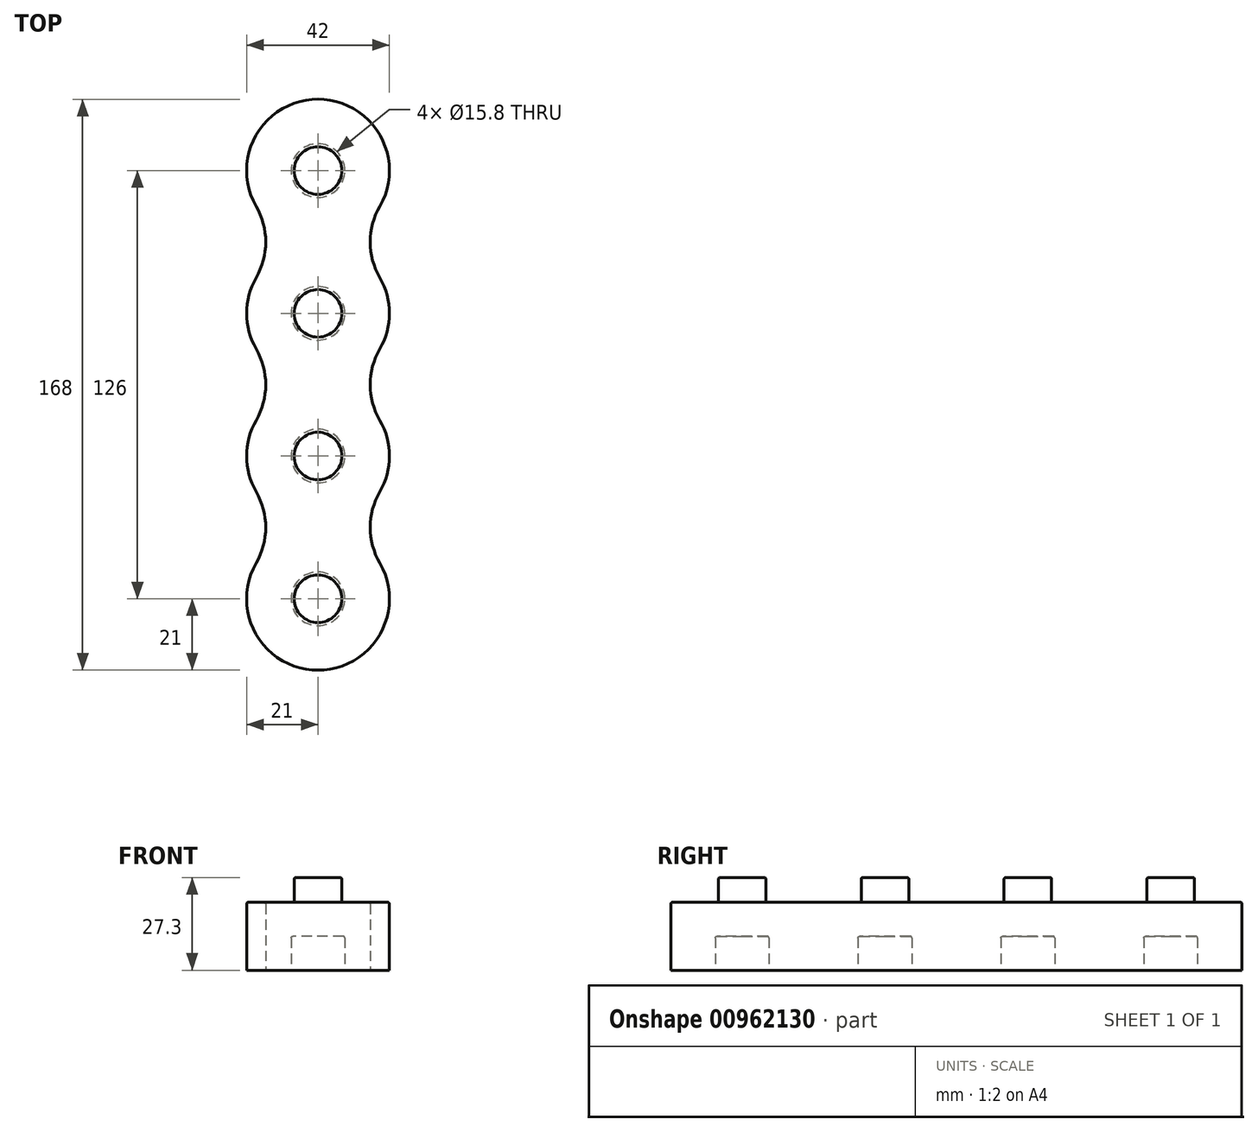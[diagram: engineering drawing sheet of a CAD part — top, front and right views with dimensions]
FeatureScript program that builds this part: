
annotation { "Feature Type Name" : "Feature", "Feature Type Description" : "" }
export const myFeature = defineFeature(function(context is Context, id is Id, definition is map)
    precondition{}
    {
        {
            assignVariable(context, id + "F0", {"name" : "inner_circle_extrude", "anyValue" : 10});
        }
        {
            assignVariable(context, id + "F1", {"name" : "nipple_circle_extrude", "anyValue" : 7.3});
        }
        {
            assignVariable(context, id + "F2", {"name" : "outer_circle_extrude", "anyValue" : 20});
        }
        {
            assignVariable(context, id + "F3", {"name" : "fillet", "anyValue" : 0.5});
        }
        {
            var Q0;
            Q0=qCreatedBy(makeId("Top.planeOp"),FACE);
            var sketch = newSketch(context, id + "F4", { "sketchPlane" : qUnion([Q0])});
            skCircle(sketch, "E0", {"center": v(0, 42) * mm, "radius": 7.9 * mm});
            skCircle(sketch, "E1", {"center": v(0, 0) * mm, "radius": 7.9 * mm});
            skArc(sketch, "E2.converted", {"start": v(18.19, 31.5) * mm, "mid": v(21, 42) * mm, "end": v(18.19, 52.5) * mm});
            skArc(sketch, "E3.converted", {"start": v(-18.19, 10.5) * mm, "mid": v(0, -21) * mm, "end": v(18.19, 10.5) * mm});
            skPoint(sketch, "E4.orphan", {"position": v(-18.87, 9.22) * mm});
            skArc(sketch, "E5", {"start": v(-18.19, 10.5) * mm, "mid": v(-15.37, 21) * mm, "end": v(-18.19, 31.5) * mm});
            skArc(sketch, "E6.MirrorC", {"start": v(18.19, 10.5) * mm, "mid": v(15.37, 21) * mm, "end": v(18.19, 31.5) * mm});
            skArc(sketch, "E7", {"start": v(-18.19, 94.5) * mm, "mid": v(-21, 84) * mm, "end": v(-18.19, 73.5) * mm});
            skArc(sketch, "E8", {"start": v(-18.19, 52.5) * mm, "mid": v(-15.37, 63) * mm, "end": v(-18.19, 73.5) * mm});
            skArc(sketch, "E9", {"start": v(18.19, 73.5) * mm, "mid": v(15.37, 63) * mm, "end": v(18.19, 52.5) * mm});
            skArc(sketch, "E10", {"start": v(18.19, 115.5) * mm, "mid": v(0, 147) * mm, "end": v(-18.19, 115.5) * mm});
            skArc(sketch, "E11", {"start": v(-18.19, 94.5) * mm, "mid": v(-15.37, 105) * mm, "end": v(-18.19, 115.5) * mm});
            skArc(sketch, "E12", {"start": v(18.19, 115.5) * mm, "mid": v(15.37, 105) * mm, "end": v(18.19, 94.5) * mm});
            skCircle(sketch, "E13", {"center": v(0, 84) * mm, "radius": 7.9 * mm});
            skCircle(sketch, "E14", {"center": v(0, 126) * mm, "radius": 7.9 * mm});
            skArc(sketch, "E15.trimOffspring", {"start": v(18.19, 73.5) * mm, "mid": v(21, 84) * mm, "end": v(18.19, 94.5) * mm});
            skArc(sketch, "E16.trimOffspring", {"start": v(-18.19, 52.5) * mm, "mid": v(-21, 42) * mm, "end": v(-18.19, 31.5) * mm});
            skSolve(sketch);
        }
        {
            var Q0;
            Q0=makeQuery(id+"F4.imprint","IMPRINT",FACE,{"disambiguationData":[TD([[makeQuery(id+"F4.imprint","IMPRINT",EDGE,{"derivedFrom":sQuery(id+"F4.wireOp",EDGE,"ScaTM9CG-l0WX-AUfX-dH3G-diZ5i2Zft3Bz")}),1.0]])]});
            var Q1;
            Q1=makeQuery(id+"F4.imprint","IMPRINT",FACE,{"disambiguationData":[TD([[makeQuery(id+"F4.imprint","IMPRINT",EDGE,{"derivedFrom":sQuery(id+"F4.wireOp",EDGE,"E0")}),1.0]])]});
            var Q2;
            Q2=makeQuery(id+"F4.imprint","IMPRINT",FACE,{"disambiguationData":[TD([[makeQuery(id+"F4.imprint","IMPRINT",EDGE,{"derivedFrom":sQuery(id+"F4.wireOp",EDGE,"E1")}),1.0]])]});
            var Q3;
            Q3=makeQuery(id+"F4.imprint","IMPRINT",FACE,{"disambiguationData":[TD([[makeQuery(id+"F4.imprint","IMPRINT",EDGE,{"derivedFrom":sQuery(id+"F4.wireOp",EDGE,"E0")}),-1.0]])]});
            var Q4;
            Q4=makeQuery(id+"F4.imprint","IMPRINT",FACE,{"disambiguationData":[TD([[makeQuery(id+"F4.imprint","IMPRINT",EDGE,{"derivedFrom":sQuery(id+"F4.wireOp",EDGE,"E14")}),1.0]])]});
            var Q5;
            Q5=makeQuery(id+"F4.imprint","IMPRINT",FACE,{"disambiguationData":[TD([[makeQuery(id+"F4.imprint","IMPRINT",EDGE,{"derivedFrom":sQuery(id+"F4.wireOp",EDGE,"E13")}),1.0]])]});
            extrude(context, id + "F5", {"entities" : qUnion([Q0, Q1, Q2, Q3, Q4, Q5]), "depth" : (getVariable(context, 'outer_circle_extrude')) * mm, "offsetDistance" : 25 * mm});
        }
        {
            var Q0;
            Q0=makeQuery(id+"F4.imprint","IMPRINT",FACE,{"disambiguationData":[TD([[makeQuery(id+"F4.imprint","IMPRINT",EDGE,{"derivedFrom":sQuery(id+"F4.wireOp",EDGE,"E0")}),1.0]])]});
            var Q1;
            Q1=makeQuery(id+"F4.imprint","IMPRINT",FACE,{"disambiguationData":[TD([[makeQuery(id+"F4.imprint","IMPRINT",EDGE,{"derivedFrom":sQuery(id+"F4.wireOp",EDGE,"E1")}),1.0]])]});
            var Q2;
            Q2=makeQuery(id+"F4.imprint","IMPRINT",FACE,{"disambiguationData":[TD([[makeQuery(id+"F4.imprint","IMPRINT",EDGE,{"derivedFrom":sQuery(id+"F4.wireOp",EDGE,"E13")}),1.0]])]});
            var Q3;
            Q3=makeQuery(id+"F4.imprint","IMPRINT",FACE,{"disambiguationData":[TD([[makeQuery(id+"F4.imprint","IMPRINT",EDGE,{"derivedFrom":sQuery(id+"F4.wireOp",EDGE,"E14")}),1.0]])]});
            extrude(context, id + "F6", {"entities" : qUnion([Q0, Q1, Q2, Q3]), "operationType" : NewBodyOperationType.REMOVE, "depth" : (getVariable(context, 'inner_circle_extrude')) * mm, "offsetDistance" : 25 * mm});
        }
        {
            var Q0;
            Q0=makeQuery(id+"F5.opExtrude","CAP_FACE",FACE,{"disambiguationData":[OSD([sQuery(id+"F4.wireOp",EDGE,"E2.converted"),sQuery(id+"F4.wireOp",EDGE,"E3.converted"),sQuery(id+"F4.wireOp",EDGE,"E5"),sQuery(id+"F4.wireOp",EDGE,"E6.MirrorC")])],"isStart":false});
            var sketch = newSketch(context, id + "F7", { "sketchPlane" : qUnion([Q0])});
            skCircle(sketch, "E17", {"center": v(0, 0) * mm, "radius": 7 * mm});
            skCircle(sketch, "E18", {"center": v(0, 42) * mm, "radius": 7 * mm});
            skCircle(sketch, "E19", {"center": v(0, 84) * mm, "radius": 7 * mm});
            skCircle(sketch, "E20", {"center": v(0, 126) * mm, "radius": 7 * mm});
            skSolve(sketch);
        }
        {
            var Q0;
            Q0=makeQuery(id+"F7.imprint","IMPRINT",FACE,{"disambiguationData":[TD([[makeQuery(id+"F7.imprint","IMPRINT",EDGE,{"derivedFrom":sQuery(id+"F7.wireOp",EDGE,"E17")}),1.0]])]});
            var Q1;
            Q1=makeQuery(id+"F7.imprint","IMPRINT",FACE,{"disambiguationData":[TD([[makeQuery(id+"F7.imprint","IMPRINT",EDGE,{"derivedFrom":sQuery(id+"F7.wireOp",EDGE,"Dg55u7MG-Wcnn-qXMQ-j3jR-78wnB7IFwmOc")}),1.0]])]});
            var Q2;
            Q2=makeQuery(id+"F7.imprint","IMPRINT",FACE,{"disambiguationData":[TD([[makeQuery(id+"F7.imprint","IMPRINT",EDGE,{"derivedFrom":sQuery(id+"F7.wireOp",EDGE,"E18")}),1.0]])]});
            var Q3;
            Q3=makeQuery(id+"F7.imprint","IMPRINT",FACE,{"disambiguationData":[TD([[makeQuery(id+"F7.imprint","IMPRINT",EDGE,{"derivedFrom":sQuery(id+"F7.wireOp",EDGE,"E19")}),1.0]])]});
            var Q4;
            Q4=makeQuery(id+"F7.imprint","IMPRINT",FACE,{"disambiguationData":[TD([[makeQuery(id+"F7.imprint","IMPRINT",EDGE,{"derivedFrom":sQuery(id+"F7.wireOp",EDGE,"E20")}),1.0]])]});
            extrude(context, id + "F8", {"entities" : qUnion([Q0, Q1, Q2, Q3, Q4]), "operationType" : NewBodyOperationType.ADD, "depth" : (getVariable(context, 'nipple_circle_extrude')) * mm, "offsetDistance" : 25 * mm});
        }
        {
            var Q0;
            Q0=makeQuery(id+"F8.opExtrude","CAP_EDGE",EDGE,{"disambiguationData":[OSD([sQuery(id+"F7.wireOp",EDGE,"E17")])],"isStart":false});
            var Q1;
            Q1=makeQuery(id+"F5.opExtrude","CAP_EDGE",EDGE,{"disambiguationData":[OSD([sQuery(id+"F4.wireOp",EDGE,"ScaTM9CG-l0WX-AUfX-dH3G-diZ5i2Zft3Bz")])],"isStart":false});
            var Q2;
            Q2=makeQuery(id+"F5.opExtrude","CAP_EDGE",EDGE,{"disambiguationData":[OSD([sQuery(id+"F4.wireOp",EDGE,"ScaTM9CG-l0WX-AUfX-dH3G-diZ5i2Zft3Bz")])],"isStart":true});
            var Q3;
            Q3=makeQuery(id+"F6.boolean.opBoolean","COPY",EDGE,{"derivedFrom":makeQuery(id+"F6.opExtrude","CAP_EDGE",EDGE,{"disambiguationData":[OSD([sQuery(id+"F4.wireOp",EDGE,"E0")])],"isStart":true})});
            var Q4;
            Q4=makeQuery(id+"F6.boolean.opBoolean","COPY",FACE,{"derivedFrom":makeQuery(id+"F6.opExtrude","CAP_FACE",FACE,{"disambiguationData":[OSD([sQuery(id+"F4.wireOp",EDGE,"E0")])],"isStart":false})});
            var Q5;
            Q5=makeQuery(id+"F6.boolean.opBoolean","COPY",EDGE,{"derivedFrom":makeQuery(id+"F6.opExtrude","CAP_EDGE",EDGE,{"disambiguationData":[OSD([sQuery(id+"F4.wireOp",EDGE,"E1")])],"isStart":true})});
            var Q6;
            Q6=makeQuery(id+"F6.boolean.opBoolean","COPY",EDGE,{"derivedFrom":makeQuery(id+"F6.opExtrude","CAP_EDGE",EDGE,{"disambiguationData":[OSD([sQuery(id+"F4.wireOp",EDGE,"E1")])],"isStart":false})});
            var Q7;
            Q7=makeQuery(id+"F8.opExtrude","CAP_EDGE",EDGE,{"disambiguationData":[OSD([sQuery(id+"F7.wireOp",EDGE,"Dg55u7MG-Wcnn-qXMQ-j3jR-78wnB7IFwmOc")])],"isStart":true});
            var Q8;
            Q8=makeQuery(id+"F8.opExtrude","CAP_EDGE",EDGE,{"disambiguationData":[OSD([sQuery(id+"F7.wireOp",EDGE,"Dg55u7MG-Wcnn-qXMQ-j3jR-78wnB7IFwmOc")])],"isStart":false});
            var Q9;
            Q9=makeQuery(id+"F8.opExtrude","CAP_EDGE",EDGE,{"disambiguationData":[OSD([sQuery(id+"F7.wireOp",EDGE,"E18")])],"isStart":false});
            var Q10;
            Q10=makeQuery(id+"F8.opExtrude","CAP_EDGE",EDGE,{"disambiguationData":[OSD([sQuery(id+"F7.wireOp",EDGE,"E18")])],"isStart":true});
            var Q11;
            Q11=makeQuery(id+"F5.opExtrude","CAP_EDGE",EDGE,{"disambiguationData":[OSD([sQuery(id+"F4.wireOp",EDGE,"E2.converted")])],"isStart":false});
            var Q12;
            Q12=makeQuery(id+"F8.opExtrude","CAP_EDGE",EDGE,{"disambiguationData":[OSD([sQuery(id+"F7.wireOp",EDGE,"E19")])],"isStart":false});
            var Q13;
            Q13=makeQuery(id+"F8.opExtrude","CAP_EDGE",EDGE,{"disambiguationData":[OSD([sQuery(id+"F7.wireOp",EDGE,"E19")])],"isStart":true});
            var Q14;
            Q14=makeQuery(id+"F8.opExtrude","CAP_EDGE",EDGE,{"disambiguationData":[OSD([sQuery(id+"F7.wireOp",EDGE,"E20")])],"isStart":false});
            var Q15;
            Q15=makeQuery(id+"F8.opExtrude","CAP_EDGE",EDGE,{"disambiguationData":[OSD([sQuery(id+"F7.wireOp",EDGE,"E20")])],"isStart":true});
            var Q16;
            Q16=makeQuery(id+"F6.boolean.opBoolean","COPY",EDGE,{"derivedFrom":makeQuery(id+"F6.opExtrude","CAP_EDGE",EDGE,{"disambiguationData":[OSD([sQuery(id+"F4.wireOp",EDGE,"E13")])],"isStart":false})});
            var Q17;
            Q17=makeQuery(id+"F6.boolean.opBoolean","COPY",EDGE,{"derivedFrom":makeQuery(id+"F6.opExtrude","CAP_EDGE",EDGE,{"disambiguationData":[OSD([sQuery(id+"F4.wireOp",EDGE,"E13")])],"isStart":true})});
            var Q18;
            Q18=makeQuery(id+"F6.boolean.opBoolean","COPY",EDGE,{"derivedFrom":makeQuery(id+"F6.opExtrude","CAP_EDGE",EDGE,{"disambiguationData":[OSD([sQuery(id+"F4.wireOp",EDGE,"E14")])],"isStart":false})});
            var Q19;
            Q19=makeQuery(id+"F6.boolean.opBoolean","COPY",EDGE,{"derivedFrom":makeQuery(id+"F6.opExtrude","CAP_EDGE",EDGE,{"disambiguationData":[OSD([sQuery(id+"F4.wireOp",EDGE,"E14")])],"isStart":true})});
            var Q20;
            Q20=makeQuery(id+"F8.opExtrude","CAP_EDGE",EDGE,{"disambiguationData":[OSD([sQuery(id+"F7.wireOp",EDGE,"E17")])],"isStart":true});
            fillet(context, id + "F9", {"entities" : qUnion([Q0, Q1, Q2, Q3, Q4, Q5, Q6, Q7, Q8, Q9, Q10, Q11, Q12, Q13, Q14, Q15, Q16, Q17, Q18, Q19, Q20]), "radius" : (getVariable(context, 'fillet')) * mm, "tangentPropagation" : true, "allowEdgeOverflow" : false});
        }
    });
